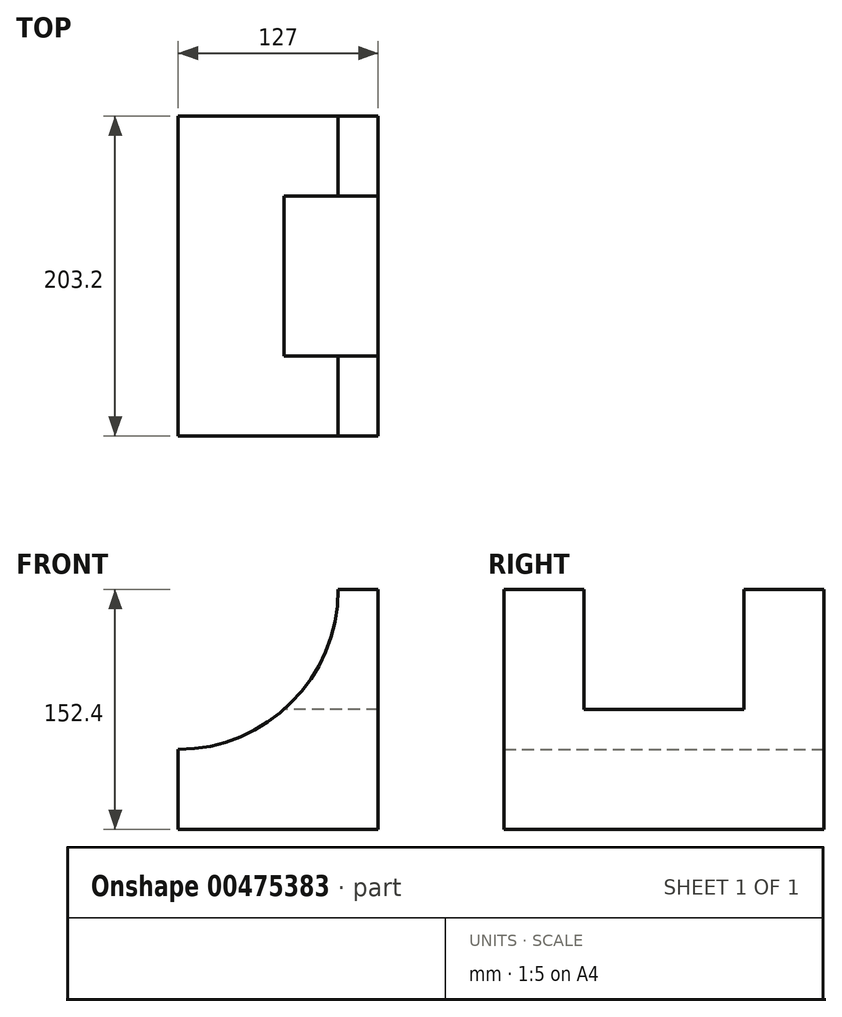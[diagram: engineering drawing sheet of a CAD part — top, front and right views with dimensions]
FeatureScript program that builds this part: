
annotation { "Feature Type Name" : "Feature", "Feature Type Description" : "" }
export const myFeature = defineFeature(function(context is Context, id is Id, definition is map)
    precondition{}
    {
        {
            var Q0;
            Q0=qCreatedBy(makeId("Front.planeOp"),FACE);
            var sketch = newSketch(context, id + "F0", { "sketchPlane" : qUnion([Q0])});
            skLineSegment(sketch, "E0.bottom", {"start": v(0, 0) * mm, "end": v(127, 0) * mm});
            skLineSegment(sketch, "E0.top", {"start": v(0, 152.4) * mm, "end": v(127, 152.4) * mm});
            skLineSegment(sketch, "E0.left", {"start": v(0, 0) * mm, "end": v(0, 152.4) * mm});
            skLineSegment(sketch, "E0.right", {"start": v(127, 0) * mm, "end": v(127, 152.4) * mm});
            skCircle(sketch, "E1", {"center": v(0, 152.4) * mm, "radius": 101.6 * mm});
            skLineSegment(sketch, "E2", {"start": v(127, 76.2) * mm, "end": v(25.4, 76.2) * mm});
            skLineSegment(sketch, "E3", {"start": v(25.4, 76.2) * mm, "end": v(25.4, 152.4) * mm});
            skSolve(sketch);
        }
        {
            var Q0;
            {var subQ0=sQuery(id+"F0.wireOp",EDGE,"E0.right");var subQ1=sQuery(id+"F0.wireOp",EDGE,"E0.top");var subQ2=makeQuery(id+"F0.imprint","INTERSECT",VERTEX,{"derivedFrom":[subQ1,subQ0]});Q0=makeQuery(id+"F0.imprint","IMPRINT",FACE,{"disambiguationData":[TD([[makeQuery(id+"F0.imprint","IMPRINT",EDGE,{"disambiguationData":[TD([[subQ2,1.0]])],"derivedFrom":subQ1}),-1.0]])]});}
            var Q1;
            {var subQ1=sQuery(id+"F0.wireOp",EDGE,"E0.bottom");Q1=makeQuery(id+"F0.imprint","IMPRINT",FACE,{"disambiguationData":[TD([[makeQuery(id+"F0.imprint","IMPRINT",EDGE,{"derivedFrom":subQ1}),1.0]])]});}
            extrude(context, id + "F1", {"entities" : qUnion([Q0, Q1]), "depth" : 203.2 * mm, "offsetDistance" : 25.4 * mm});
        }
        {
            var Q0;
            {var subQ0=sQuery(id+"F0.wireOp",EDGE,"E2");Q0=makeQuery(id+"F0.imprint","IMPRINT",FACE,{"disambiguationData":[TD([[makeQuery(id+"F0.imprint","IMPRINT",EDGE,{"derivedFrom":subQ0}),-1.0]])]});}
            var Q1;
            {var subQ0=sQuery(id+"F0.wireOp",EDGE,"E3");var subQ1=sQuery(id+"F0.wireOp",EDGE,"E0.top");var subQ2=makeQuery(id+"F0.imprint","INTERSECT",VERTEX,{"derivedFrom":[subQ1,subQ0]});Q1=makeQuery(id+"F0.imprint","IMPRINT",FACE,{"disambiguationData":[TD([[makeQuery(id+"F0.imprint","IMPRINT",EDGE,{"disambiguationData":[TD([[subQ2,-1.0]])],"derivedFrom":subQ1}),-1.0]])]});}
            extrude(context, id + "F2", {"entities" : qUnion([Q0, Q1]), "operationType" : NewBodyOperationType.REMOVE, "depth" : 152.4 * mm, "offsetDistance" : 25.4 * mm, "hasSecondDirection" : true, "secondDirectionOppositeDirection" : false, "secondDirectionDepth" : 50.8 * mm});
        }
    });
